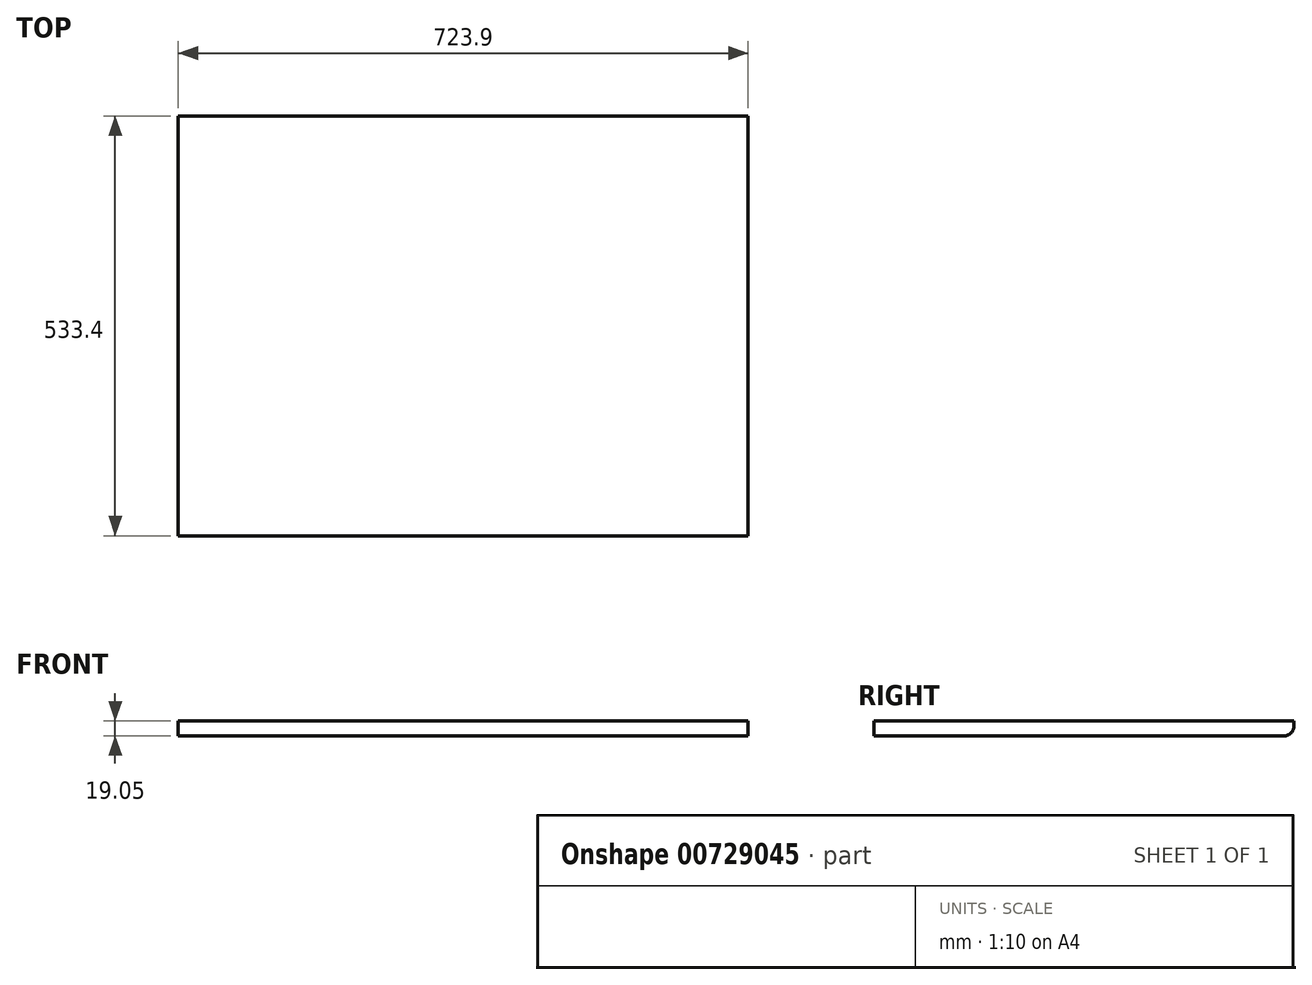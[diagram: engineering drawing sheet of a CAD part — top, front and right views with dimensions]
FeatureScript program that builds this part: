
annotation { "Feature Type Name" : "Feature", "Feature Type Description" : "" }
export const myFeature = defineFeature(function(context is Context, id is Id, definition is map)
    precondition{}
    {
        {
            var Q0;
            Q0=qCreatedBy(makeId("Top.planeOp"),FACE);
            var sketch = newSketch(context, id + "F0", { "sketchPlane" : qUnion([Q0])});
            skLineSegment(sketch, "E0.bottom", {"start": v(361.95, -266.7) * mm, "end": v(-361.95, -266.7) * mm});
            skLineSegment(sketch, "E0.top", {"start": v(361.95, 266.7) * mm, "end": v(-361.95, 266.7) * mm});
            skLineSegment(sketch, "E0.left", {"start": v(361.95, -266.7) * mm, "end": v(361.95, 266.7) * mm});
            skLineSegment(sketch, "E0.right", {"start": v(-361.95, -266.7) * mm, "end": v(-361.95, 266.7) * mm});
            skPoint(sketch, "E0.middle", {"position": v(0, 0) * mm});
            skSolve(sketch);
        }
        {
            var Q0;
            Q0 = qSketchRegion(id + "F0", true);
            extrude(context, id + "F1", {"entities" : qUnion([Q0]), "depth" : 19.05 * mm, "offsetDistance" : 25.4 * mm});
        }
        {
            var Q0;
            Q0=makeQuery(id+"F1.opExtrude","CAP_EDGE",EDGE,{"disambiguationData":[OSD([sQuery(id+"F0.wireOp",EDGE,"E0.top")])],"isStart":true});
            fillet(context, id + "F2", {"entities" : qUnion([Q0]), "radius" : 12.7 * mm, "tangentPropagation" : true, "allowEdgeOverflow" : false});
        }
    });
